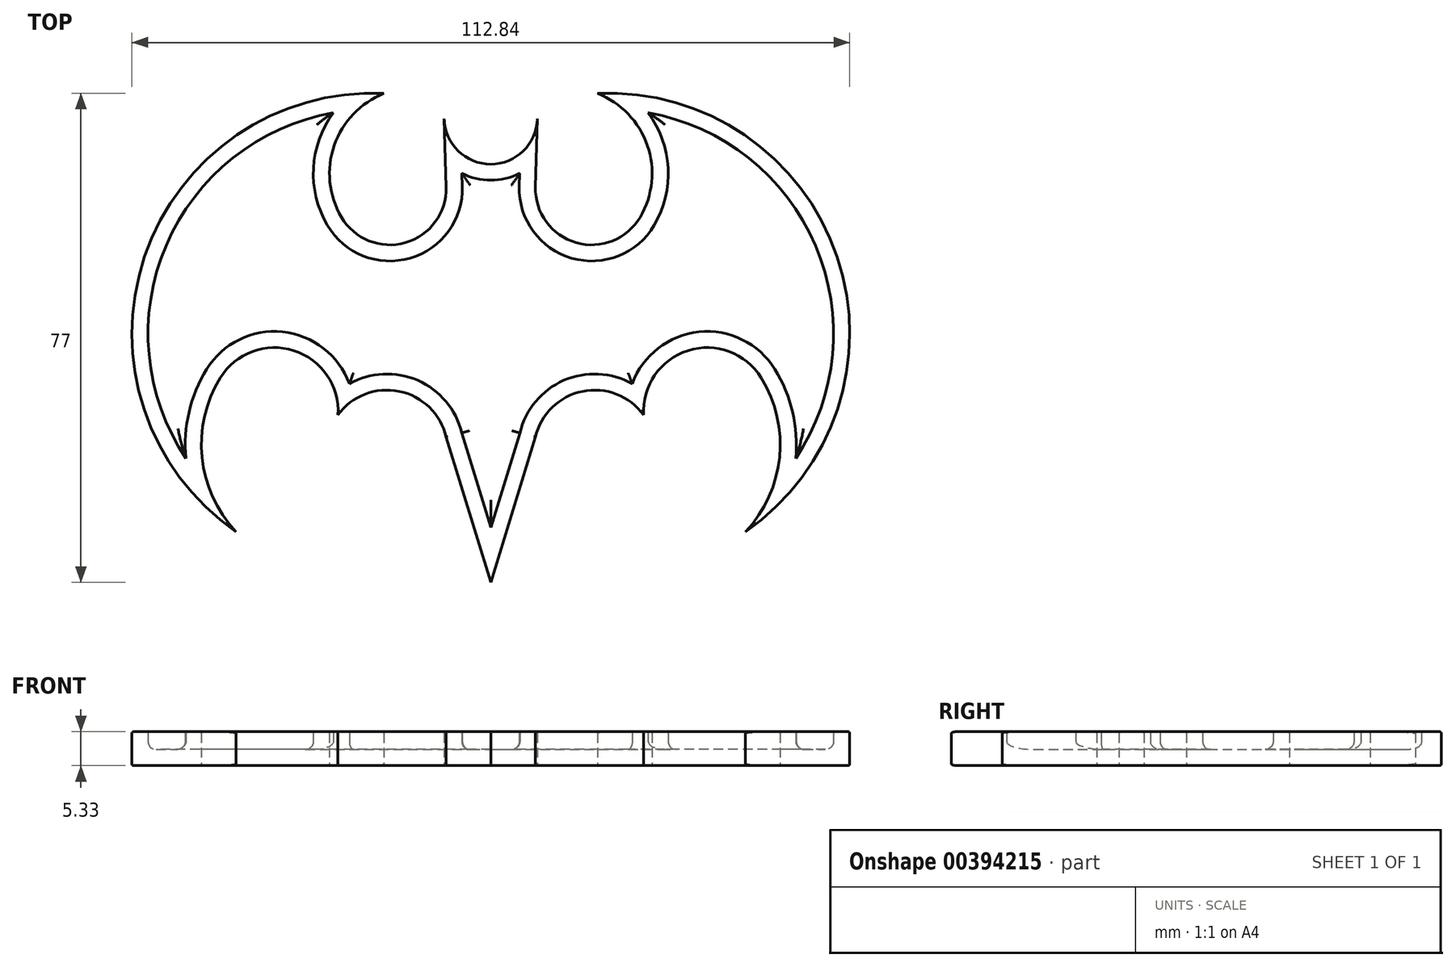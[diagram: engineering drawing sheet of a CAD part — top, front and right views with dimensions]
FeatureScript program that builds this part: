
annotation { "Feature Type Name" : "Feature", "Feature Type Description" : "" }
export const myFeature = defineFeature(function(context is Context, id is Id, definition is map)
    precondition{}
    {
        {
            var Q0;
            Q0=qCreatedBy(makeId("Top.planeOp"),FACE);
            var sketch = newSketch(context, id + "F0", { "sketchPlane" : qUnion([Q0])});
            skArc(sketch, "E0", {"start": v(-7.33, 18.25) * mm, "mid": v(-5.1, 13.2) * mm, "end": v(0, 11.13) * mm});
            skLineSegment(sketch, "E1", {"start": v(-7.33, 18.25) * mm, "end": v(-7.02, 7.53) * mm});
            skArc(sketch, "E2", {"start": v(-7.02, 7.53) * mm, "mid": v(-13.42, -1.23) * mm, "end": v(-23.5, 2.8) * mm});
            skArc(sketch, "E3", {"start": v(-23.5, 2.8) * mm, "mid": v(-24.61, 14.07) * mm, "end": v(-16.78, 22.26) * mm});
            skArc(sketch, "E4", {"start": v(-16.78, 22.26) * mm, "mid": v(-54.44, -3.46) * mm, "end": v(-40.04, -46.73) * mm});
            skArc(sketch, "E5", {"start": v(-42.5, -22.49) * mm, "mid": v(-45.4, -35.02) * mm, "end": v(-40.04, -46.73) * mm});
            skPoint(sketch, "E6.third.point", {"position": v(-25.5, -22.49) * mm});
            skLineSegment(sketch, "E7", {"start": v(-7.02, 7.53) * mm, "end": v(-7.02, 7.02) * mm, "construction": true});
            skArc(sketch, "E8", {"start": v(-7.02, -31.83) * mm, "mid": v(-14.4, -24.63) * mm, "end": v(-24.03, -28.35) * mm});
            skPoint(sketch, "E8.second.point", {"position": v(-7.02, -36.13) * mm});
            skPoint(sketch, "E8.third.point", {"position": v(-15.86, -43.52) * mm});
            skFitSpline(sketch, "E9", {"points": [v(-7.02, -31.83) * mm, v(0, -54.7) * mm], "startDerivative": vector(7.02, -22.88) * mm, "endDerivative": vector(7.02, -22.88) * mm});
            skArc(sketch, "E10.trimOffspring", {"start": v(-24.03, -28.35) * mm, "mid": v(-30.98, -18.22) * mm, "end": v(-42.5, -22.49) * mm});
            skPoint(sketch, "E11", {"position": v(0, 11.13) * mm});
            skArc(sketch, "E12.MirrorCS", {"start": v(7.33, 18.25) * mm, "mid": v(5.1, 13.2) * mm, "end": v(0, 11.13) * mm});
            skLineSegment(sketch, "E13.MirrorCS", {"start": v(7.33, 18.25) * mm, "end": v(7.02, 7.53) * mm});
            skArc(sketch, "E14.MirrorCS", {"start": v(7.02, 7.53) * mm, "mid": v(13.42, -1.23) * mm, "end": v(23.5, 2.8) * mm});
            skArc(sketch, "E15.MirrorCS", {"start": v(23.5, 2.8) * mm, "mid": v(24.61, 14.07) * mm, "end": v(16.78, 22.26) * mm});
            skArc(sketch, "E16.MirrorCS", {"start": v(16.78, 22.26) * mm, "mid": v(54.44, -3.46) * mm, "end": v(40.04, -46.73) * mm});
            skArc(sketch, "E17.MirrorCS", {"start": v(42.5, -22.49) * mm, "mid": v(45.4, -35.02) * mm, "end": v(40.04, -46.73) * mm});
            skArc(sketch, "E18.MirrorCS", {"start": v(24.03, -28.35) * mm, "mid": v(30.98, -18.22) * mm, "end": v(42.5, -22.49) * mm});
            skArc(sketch, "E19.MirrorCS", {"start": v(7.02, -31.83) * mm, "mid": v(14.4, -24.63) * mm, "end": v(24.03, -28.35) * mm});
            skFitSpline(sketch, "E20.MirrorCS", {"points": [v(7.02, -31.83) * mm, v(0, -54.7) * mm], "startDerivative": vector(-7.02, -22.88) * mm, "endDerivative": vector(-7.02, -22.88) * mm});
            skPoint(sketch, "E21.orphan", {"position": v(-15.86, -1.58) * mm});
            skPoint(sketch, "E22.orphan", {"position": v(0, -28.3) * mm});
            skPoint(sketch, "E23.orphan", {"position": v(-7.02, -54.26) * mm});
            skPoint(sketch, "E24.end.orphan", {"position": v(-15.86, -54.26) * mm});
            skSolve(sketch);
        }
        {
            var Q0;
            Q0 = qSketchRegion(id + "F0", true);
            extrude(context, id + "F1", {"entities" : qUnion([Q0]), "depth" : 5.33 * mm});
        }
        {
            var Q0;
            Q0=makeQuery(id+"F1.opExtrude","CAP_EDGE",EDGE,{"disambiguationData":[OSD([sQuery(id+"F0.wireOp",EDGE,"E10.trimOffspring")])],"isStart":false});
            var Q1;
            Q1=makeQuery(id+"F1.opExtrude","CAP_FACE",FACE,{"disambiguationData":[OSD([sQuery(id+"F0.wireOp",EDGE,"E0"),sQuery(id+"F0.wireOp",EDGE,"E1"),sQuery(id+"F0.wireOp",EDGE,"E2"),sQuery(id+"F0.wireOp",EDGE,"E3"),sQuery(id+"F0.wireOp",EDGE,"E4"),sQuery(id+"F0.wireOp",EDGE,"E5"),sQuery(id+"F0.wireOp",EDGE,"E8"),sQuery(id+"F0.wireOp",EDGE,"E9"),sQuery(id+"F0.wireOp",EDGE,"E10.trimOffspring"),sQuery(id+"F0.wireOp",EDGE,"E12.MirrorCS"),sQuery(id+"F0.wireOp",EDGE,"E13.MirrorCS"),sQuery(id+"F0.wireOp",EDGE,"E14.MirrorCS"),sQuery(id+"F0.wireOp",EDGE,"E15.MirrorCS"),sQuery(id+"F0.wireOp",EDGE,"E16.MirrorCS"),sQuery(id+"F0.wireOp",EDGE,"E17.MirrorCS"),sQuery(id+"F0.wireOp",EDGE,"E18.MirrorCS"),sQuery(id+"F0.wireOp",EDGE,"E19.MirrorCS"),sQuery(id+"F0.wireOp",EDGE,"E20.MirrorCS")])],"isStart":false});
            fillet(context, id + "F2", {"entities" : qUnion([Q0, Q1]), "radius" : 0.25 * mm, "tangentPropagation" : true, "allowEdgeOverflow" : false});
        }
        {
            var Q0;
            Q0=makeQuery(id+"F1.opExtrude","CAP_FACE",FACE,{"disambiguationData":[OSD([sQuery(id+"F0.wireOp",EDGE,"E0"),sQuery(id+"F0.wireOp",EDGE,"E1"),sQuery(id+"F0.wireOp",EDGE,"E2"),sQuery(id+"F0.wireOp",EDGE,"E3"),sQuery(id+"F0.wireOp",EDGE,"E4"),sQuery(id+"F0.wireOp",EDGE,"E5"),sQuery(id+"F0.wireOp",EDGE,"E8"),sQuery(id+"F0.wireOp",EDGE,"E9"),sQuery(id+"F0.wireOp",EDGE,"E10.trimOffspring"),sQuery(id+"F0.wireOp",EDGE,"E12.MirrorCS"),sQuery(id+"F0.wireOp",EDGE,"E13.MirrorCS"),sQuery(id+"F0.wireOp",EDGE,"E14.MirrorCS"),sQuery(id+"F0.wireOp",EDGE,"E15.MirrorCS"),sQuery(id+"F0.wireOp",EDGE,"E16.MirrorCS"),sQuery(id+"F0.wireOp",EDGE,"E17.MirrorCS"),sQuery(id+"F0.wireOp",EDGE,"E18.MirrorCS"),sQuery(id+"F0.wireOp",EDGE,"E19.MirrorCS"),sQuery(id+"F0.wireOp",EDGE,"E20.MirrorCS")])],"isStart":true});
            fillet(context, id + "F3", {"entities" : qUnion([Q0]), "radius" : 0.25 * mm, "tangentPropagation" : true, "allowEdgeOverflow" : false});
        }
        {
            var Q0;
            Q0=makeQuery(id+"F1.opExtrude","CAP_FACE",FACE,{"disambiguationData":[OSD([sQuery(id+"F0.wireOp",EDGE,"E0"),sQuery(id+"F0.wireOp",EDGE,"E1"),sQuery(id+"F0.wireOp",EDGE,"E2"),sQuery(id+"F0.wireOp",EDGE,"E3"),sQuery(id+"F0.wireOp",EDGE,"E4"),sQuery(id+"F0.wireOp",EDGE,"E5"),sQuery(id+"F0.wireOp",EDGE,"E8"),sQuery(id+"F0.wireOp",EDGE,"E9"),sQuery(id+"F0.wireOp",EDGE,"E10.trimOffspring"),sQuery(id+"F0.wireOp",EDGE,"E12.MirrorCS"),sQuery(id+"F0.wireOp",EDGE,"E13.MirrorCS"),sQuery(id+"F0.wireOp",EDGE,"E14.MirrorCS"),sQuery(id+"F0.wireOp",EDGE,"E15.MirrorCS"),sQuery(id+"F0.wireOp",EDGE,"E16.MirrorCS"),sQuery(id+"F0.wireOp",EDGE,"E17.MirrorCS"),sQuery(id+"F0.wireOp",EDGE,"E18.MirrorCS"),sQuery(id+"F0.wireOp",EDGE,"E19.MirrorCS"),sQuery(id+"F0.wireOp",EDGE,"E20.MirrorCS")])],"isStart":false});
            shell(context, id + "F4", {"entities" : qUnion([Q0]), "thickness" : 2.54 * mm});
        }
        {
            var Q0;
            {var subQ0=sQuery(id+"F0.wireOp",EDGE,"E3");var subQ1=makeQuery(id+"F1.opExtrude","CAP_EDGE",EDGE,{"disambiguationData":[OSD([subQ0])],"isStart":true});var subQ2=sQuery(id+"F0.wireOp",EDGE,"E20.MirrorCS");var subQ3=sQuery(id+"F0.wireOp",EDGE,"E19.MirrorCS");var subQ4=sQuery(id+"F0.wireOp",EDGE,"E18.MirrorCS");var subQ5=sQuery(id+"F0.wireOp",EDGE,"E17.MirrorCS");var subQ6=sQuery(id+"F0.wireOp",EDGE,"E16.MirrorCS");var subQ7=sQuery(id+"F0.wireOp",EDGE,"E15.MirrorCS");var subQ8=sQuery(id+"F0.wireOp",EDGE,"E14.MirrorCS");var subQ9=sQuery(id+"F0.wireOp",EDGE,"E13.MirrorCS");var subQ10=sQuery(id+"F0.wireOp",EDGE,"E12.MirrorCS");var subQ11=sQuery(id+"F0.wireOp",EDGE,"E10.trimOffspring");var subQ12=sQuery(id+"F0.wireOp",EDGE,"E9");var subQ13=sQuery(id+"F0.wireOp",EDGE,"E8");var subQ14=sQuery(id+"F0.wireOp",EDGE,"E5");var subQ15=sQuery(id+"F0.wireOp",EDGE,"E4");var subQ16=sQuery(id+"F0.wireOp",EDGE,"E2");var subQ17=sQuery(id+"F0.wireOp",EDGE,"E1");var subQ18=sQuery(id+"F0.wireOp",EDGE,"E0");Q0=makeQuery(id+"F4.opShell","OFFSET_EDGE",EDGE,{"disambiguationData":[OSD([subQ18,subQ17,subQ16,subQ0,subQ15,subQ14,subQ13,subQ12,subQ11,subQ10,subQ9,subQ8,subQ7,subQ6,subQ5,subQ4,subQ3,subQ2]),TDD([makeQuery(id+"F3.opFillet","BLEND_EDGE",EDGE,{"blendedFrom":[subQ1,makeQuery(id+"F1.opExtrude","CAP_FACE",FACE,{"disambiguationData":[OSD([subQ18,subQ17,subQ16,subQ0,subQ15,subQ14,subQ13,subQ12,subQ11,subQ10,subQ9,subQ8,subQ7,subQ6,subQ5,subQ4,subQ3,subQ2])],"isStart":true})],"blendedInto":[makeQuery(id+"F1.opExtrude","CAP_FACE",FACE,{"disambiguationData":[OSD([subQ18,subQ17,subQ16,subQ0,subQ15,subQ14,subQ13,subQ12,subQ11,subQ10,subQ9,subQ8,subQ7,subQ6,subQ5,subQ4,subQ3,subQ2])],"isStart":true})]}),makeQuery(id+"F3.opFillet","BLEND_EDGE",EDGE,{"blendedFrom":[subQ1,makeQuery(id+"F1.opExtrude","SWEPT_FACE",FACE,{"disambiguationData":[OSD([subQ0])]})],"blendedInto":[makeQuery(id+"F1.opExtrude","SWEPT_FACE",FACE,{"disambiguationData":[OSD([subQ0])]})]})])]});}
            var Q1;
            {var subQ0=sQuery(id+"F0.wireOp",EDGE,"E12.MirrorCS");var subQ1=sQuery(id+"F0.wireOp",EDGE,"E0");var subQ2=makeQuery(id+"F1.opExtrude","CAP_EDGE",EDGE,{"disambiguationData":[OSD([subQ1,subQ0])],"isStart":true});var subQ3=sQuery(id+"F0.wireOp",EDGE,"E20.MirrorCS");var subQ4=sQuery(id+"F0.wireOp",EDGE,"E19.MirrorCS");var subQ5=sQuery(id+"F0.wireOp",EDGE,"E18.MirrorCS");var subQ6=sQuery(id+"F0.wireOp",EDGE,"E17.MirrorCS");var subQ7=sQuery(id+"F0.wireOp",EDGE,"E16.MirrorCS");var subQ8=sQuery(id+"F0.wireOp",EDGE,"E15.MirrorCS");var subQ9=sQuery(id+"F0.wireOp",EDGE,"E14.MirrorCS");var subQ10=sQuery(id+"F0.wireOp",EDGE,"E13.MirrorCS");var subQ11=sQuery(id+"F0.wireOp",EDGE,"E10.trimOffspring");var subQ12=sQuery(id+"F0.wireOp",EDGE,"E9");var subQ13=sQuery(id+"F0.wireOp",EDGE,"E8");var subQ14=sQuery(id+"F0.wireOp",EDGE,"E5");var subQ15=sQuery(id+"F0.wireOp",EDGE,"E4");var subQ16=sQuery(id+"F0.wireOp",EDGE,"E3");var subQ17=sQuery(id+"F0.wireOp",EDGE,"E2");var subQ18=sQuery(id+"F0.wireOp",EDGE,"E1");Q1=makeQuery(id+"F4.opShell","OFFSET_EDGE",EDGE,{"disambiguationData":[OSD([subQ1,subQ18,subQ17,subQ16,subQ15,subQ14,subQ13,subQ12,subQ11,subQ0,subQ10,subQ9,subQ8,subQ7,subQ6,subQ5,subQ4,subQ3]),TDD([makeQuery(id+"F3.opFillet","BLEND_EDGE",EDGE,{"blendedFrom":[subQ2,makeQuery(id+"F1.opExtrude","CAP_FACE",FACE,{"disambiguationData":[OSD([subQ1,subQ18,subQ17,subQ16,subQ15,subQ14,subQ13,subQ12,subQ11,subQ0,subQ10,subQ9,subQ8,subQ7,subQ6,subQ5,subQ4,subQ3])],"isStart":true})],"blendedInto":[makeQuery(id+"F1.opExtrude","CAP_FACE",FACE,{"disambiguationData":[OSD([subQ1,subQ18,subQ17,subQ16,subQ15,subQ14,subQ13,subQ12,subQ11,subQ0,subQ10,subQ9,subQ8,subQ7,subQ6,subQ5,subQ4,subQ3])],"isStart":true})]}),makeQuery(id+"F3.opFillet","BLEND_EDGE",EDGE,{"blendedFrom":[subQ2,makeQuery(id+"F1.opExtrude","SWEPT_FACE",FACE,{"disambiguationData":[OSD([subQ1,subQ0])]})],"blendedInto":[makeQuery(id+"F1.opExtrude","SWEPT_FACE",FACE,{"disambiguationData":[OSD([subQ1,subQ0])]})]})])]});}
            var Q2;
            Q2=makeQuery(id+"F4.opShell","OFFSET_FACE",FACE,{"disambiguationData":[OSD([sQuery(id+"F0.wireOp",EDGE,"E0"),sQuery(id+"F0.wireOp",EDGE,"E1"),sQuery(id+"F0.wireOp",EDGE,"E2"),sQuery(id+"F0.wireOp",EDGE,"E3"),sQuery(id+"F0.wireOp",EDGE,"E4"),sQuery(id+"F0.wireOp",EDGE,"E5"),sQuery(id+"F0.wireOp",EDGE,"E8"),sQuery(id+"F0.wireOp",EDGE,"E9"),sQuery(id+"F0.wireOp",EDGE,"E10.trimOffspring"),sQuery(id+"F0.wireOp",EDGE,"E12.MirrorCS"),sQuery(id+"F0.wireOp",EDGE,"E13.MirrorCS"),sQuery(id+"F0.wireOp",EDGE,"E14.MirrorCS"),sQuery(id+"F0.wireOp",EDGE,"E15.MirrorCS"),sQuery(id+"F0.wireOp",EDGE,"E16.MirrorCS"),sQuery(id+"F0.wireOp",EDGE,"E17.MirrorCS"),sQuery(id+"F0.wireOp",EDGE,"E18.MirrorCS"),sQuery(id+"F0.wireOp",EDGE,"E19.MirrorCS"),sQuery(id+"F0.wireOp",EDGE,"E20.MirrorCS")])]});
            fillet(context, id + "F5", {"entities" : qUnion([Q0, Q1, Q2]), "radius" : 1.27 * mm, "tangentPropagation" : true, "allowEdgeOverflow" : false});
        }
    });
